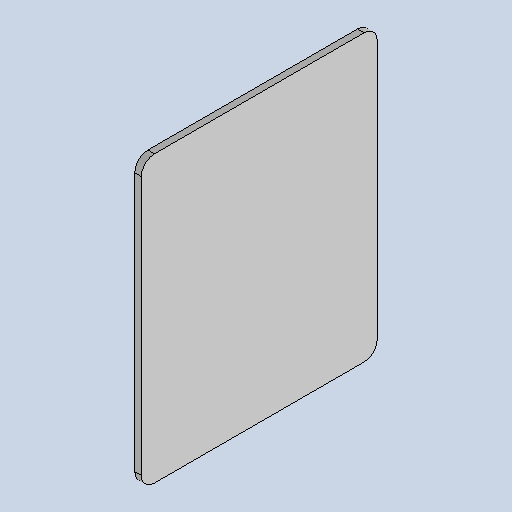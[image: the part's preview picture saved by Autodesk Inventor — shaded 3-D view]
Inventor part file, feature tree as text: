
AUTODESK INVENTOR PART (.ipt)
format: ipt  version: 2025 (Build 290162010, 162A)  size: 117,248 bytes
history: native  units: mm
features: other x2, sheet_metal_op x1, chamfer x1, sketch x1
ambient origin geometry x8: Origin, YZ Plane, XZ Plane, XY Plane, X Axis, Y Axis, Z Axis, Center Point
bodies: Solid1 (feature_tree)
feature tree (5):
  sheet_metal_op  "Face1"
  chamfer  "Corner Round1"
  sketch  "Sketch1"  dims[d0=130.0mm d1=107.582mm d2=3.0mm d3=6.0mm]
  other  "Plate1"
  other  "Definition1"
